# Revit family: Gohome_ClubLounge_3Seat_R19
name_source: partatom
category: Furniture
units: mm (PartAtom-declared; Revit-internal decimal feet)

## family parameters
Always vertical = Yes
Cut with Voids When Loaded = No
OmniClass Number = 23.40.20.00
OmniClass Title = General Furniture and Specialties
Room Calculation Point = No
Shared = No
Work Plane-Based = No

## types (2) — shared parameters
Depth = 630 mm  [stored 2.06693 ft]
Manufacturer = gohome
Seat Height = 450 mm  [stored 1.47638 ft]
Timber Leg Material = <By Category>
URL = www.gohome.com.au
Upholstery Material = <By Category>
Width = 2400 mm

## per-type parameters (varying)
| type | Height | With Screen |
| Club 3 Seat Lounge | 730 mm  [stored 2.39501 ft] | No |
| Club 3 Seat w/Screen Lounge | 1300 mm  [stored 4.26509 ft] | Yes |

note: column(s) folded — value = type name in every type: Model

note: [stored X ft] marks values corroborated as IEEE doubles in the binary element streams (Revit-internal decimal feet)

## geometry (parser evidence)
native form markers: Sweep x2
no freeform markers — native parametric forms only
